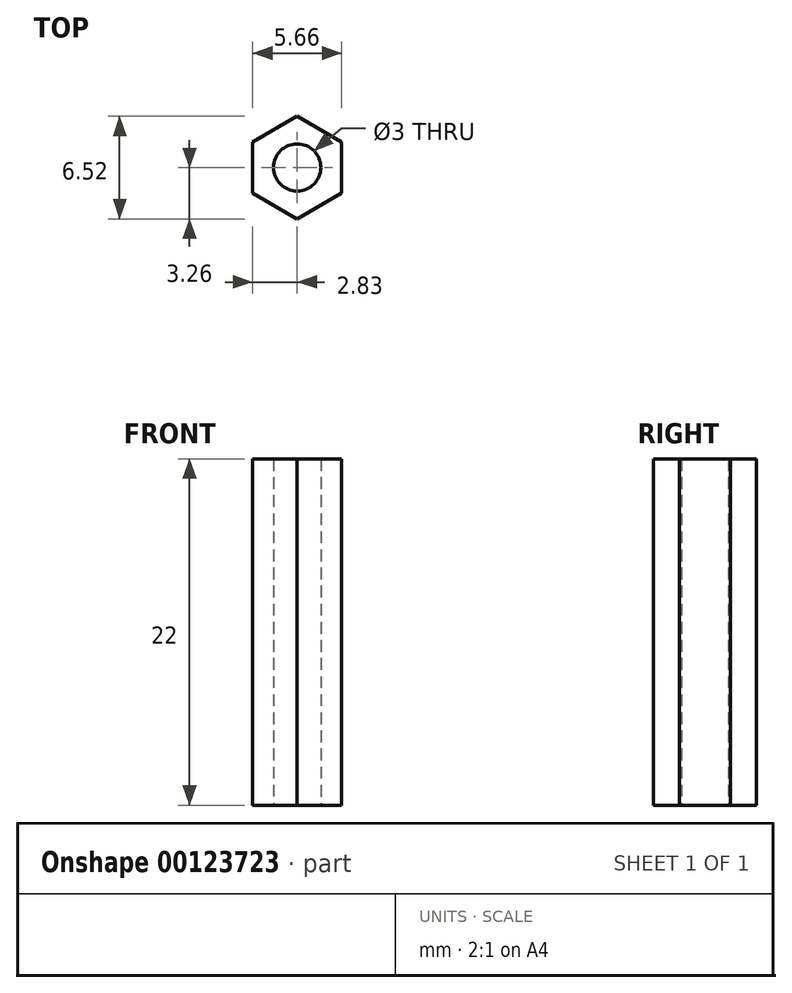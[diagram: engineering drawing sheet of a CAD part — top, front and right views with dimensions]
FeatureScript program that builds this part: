
annotation { "Feature Type Name" : "Feature", "Feature Type Description" : "" }
export const myFeature = defineFeature(function(context is Context, id is Id, definition is map)
    precondition{}
    {
        {
            var Q0;
            Q0=qCreatedBy(makeId("Top.planeOp"),FACE);
            var sketch = newSketch(context, id + "F0", { "sketchPlane" : qUnion([Q0])});
            skCircle(sketch, "E0.cCircle", {"center": v(0, 0) * mm, "radius": 2.83 * mm, "construction": true});
            skLineSegment(sketch, "E0.0", {"start": v(2.82, -1.63) * mm, "end": v(0, -3.26) * mm});
            skLineSegment(sketch, "E0.1", {"start": v(0, -3.26) * mm, "end": v(-2.83, -1.63) * mm});
            skLineSegment(sketch, "E0.2", {"start": v(-2.83, -1.63) * mm, "end": v(-2.83, 1.63) * mm});
            skLineSegment(sketch, "E0.3", {"start": v(-2.83, 1.63) * mm, "end": v(0, 3.26) * mm});
            skLineSegment(sketch, "E0.4", {"start": v(0, 3.26) * mm, "end": v(2.83, 1.63) * mm});
            skLineSegment(sketch, "E0.5", {"start": v(2.83, 1.63) * mm, "end": v(2.83, -1.63) * mm});
            skPoint(sketch, "E0.0.midPoint", {"position": v(1.41, -2.45) * mm});
            skCircle(sketch, "E1", {"center": v(0, 0) * mm, "radius": 1.5 * mm});
            skSolve(sketch);
        }
        {
            var Q0;
            Q0=qSketchRegion(id+"F0",true);
            extrude(context, id + "F1", {"entities" : qUnion([Q0]), "depth" : 22 * mm});
        }
    });
